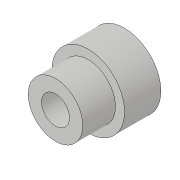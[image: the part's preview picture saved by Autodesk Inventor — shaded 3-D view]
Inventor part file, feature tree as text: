
AUTODESK INVENTOR PART (.ipt)
format: ipt  version: 2018.3 (Build 223284000, 284)  size: 95,232 bytes
history: native  units: in
note: dims shown in document units (in); Inventor stores cm internally (conversion verified against a paired STEP export)
features: extrude x3, sketch x3
ambient origin geometry x8: Origin, YZ Plane, XZ Plane, XY Plane, X Axis, Y Axis, Z Axis, Center Point
bodies: Solid1 (feature_tree)
feature tree (6):
  extrude  "Extrusion1"  Depth=0.475in TaperAngle=0.0deg
  extrude  "Extrusion2"  Depth=0.225in TaperAngle=0.0deg
  extrude  "Extrusion3"  Depth=0.2in TaperAngle=0.0deg
  sketch  "Sketch1"  dims[d0=0.5in d1=0.475in d2=0.0in]
  sketch  "Sketch2"  dims[d3=0.375in d4=0.225in d5=0.0in]
  sketch  "Sketch3"  dims[d6=0.1925in d7=0.2in d8=0.0in]
